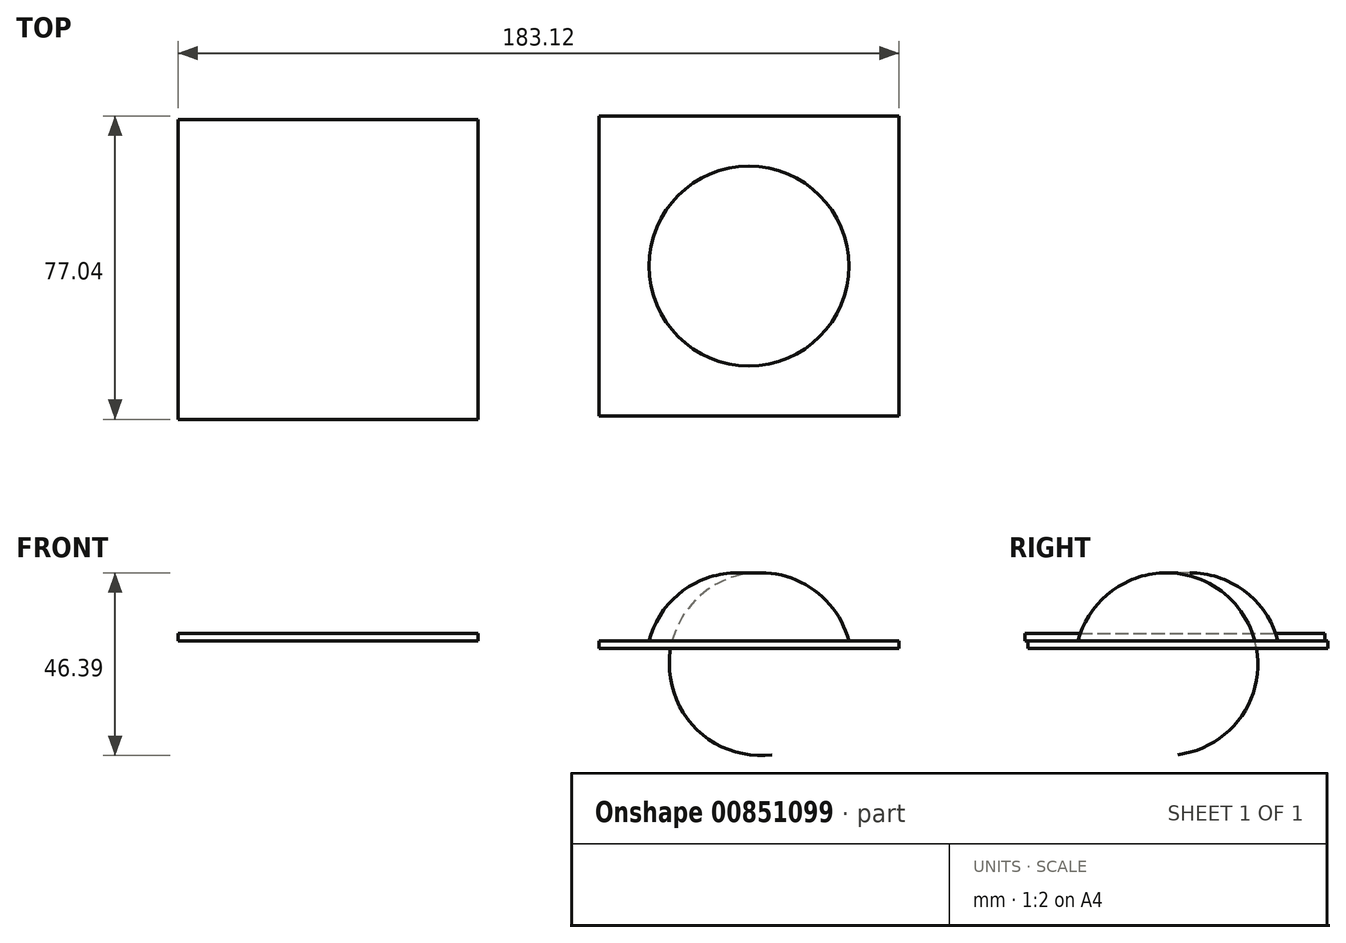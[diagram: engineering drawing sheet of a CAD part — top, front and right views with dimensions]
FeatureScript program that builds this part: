
annotation { "Feature Type Name" : "Feature", "Feature Type Description" : "" }
export const myFeature = defineFeature(function(context is Context, id is Id, definition is map)
    precondition{}
    {
        {
            var Q0;
            Q0=qCreatedBy(makeId("Front.planeOp"),FACE);
            var sketch = newSketch(context, id + "F0", { "sketchPlane" : qUnion([Q0])});
            skLineSegment(sketch, "E0", {"start": v(0, 0) * mm, "end": v(0, 17.15) * mm});
            skLineSegment(sketch, "E1", {"start": v(0, 0) * mm, "end": v(25.4, 0) * mm});
            skArc(sketch, "E2", {"start": v(25.4, 0) * mm, "mid": v(15.93, 13.36) * mm, "end": v(0, 17.14) * mm});
            skLineSegment(sketch, "E3", {"start": v(0, 75.89) * mm, "end": v(0, -74.12) * mm, "construction": true});
            skSolve(sketch);
        }
        {
            var Q0;
            Q0=makeQuery(id+"F0.imprint","IMPRINT",FACE,{"disambiguationData":[TD([[makeQuery(id+"F0.imprint","IMPRINT",EDGE,{"derivedFrom":sQuery(id+"F0.wireOp",EDGE,"E0")}),-1.0]])]});
            var Q1;
            Q1=sQuery(id+"F0.wireOp",EDGE,"E3");
            revolve(context, id + "F1", {"surfaceOperationType" : NewSurfaceOperationType.NEW, "entities" : qUnion([Q0]), "axis" : qUnion([Q1]), "revolveType" : RevolveType.FULL});
        }
        {
            var Q0;
            Q0=qCreatedBy(makeId("Top.planeOp"),FACE);
            var sketch = newSketch(context, id + "F2", { "sketchPlane" : qUnion([Q0])});
            skLineSegment(sketch, "E4.bottom", {"start": v(38.1, -38.1) * mm, "end": v(-38.1, -38.1) * mm});
            skLineSegment(sketch, "E4.top", {"start": v(38.1, 38.1) * mm, "end": v(-38.1, 38.1) * mm});
            skLineSegment(sketch, "E4.left", {"start": v(38.1, -38.1) * mm, "end": v(38.1, 38.1) * mm});
            skLineSegment(sketch, "E4.right", {"start": v(-38.1, -38.1) * mm, "end": v(-38.1, 38.1) * mm});
            skPoint(sketch, "E4.middle", {"position": v(0, 0) * mm});
            skSolve(sketch);
        }
        {
            assignVariable(context, id + "F3", {"name" : "th", "anyValue" : 1.9 * mm});
        }
        {
            var Q0;
            Q0=makeQuery(id+"F2.imprint","IMPRINT",FACE,{"disambiguationData":[TD([[makeQuery(id+"F2.imprint","IMPRINT",EDGE,{"derivedFrom":sQuery(id+"F2.wireOp",EDGE,"E4.bottom")}),-1.0]])]});
            extrude(context, id + "F4", {"entities" : qUnion([Q0]), "operationType" : NewBodyOperationType.ADD, "oppositeDirection" : true, "depth" : getVariable(context, 'th'), "offsetDistance" : 25.4 * mm});
        }
        {
            var Q0;
            Q0=qCreatedBy(makeId("Top.planeOp"),FACE);
            var sketch = newSketch(context, id + "F5", { "sketchPlane" : qUnion([Q0])});
            skLineSegment(sketch, "E5.bottom", {"start": v(-145.02, -38.94) * mm, "end": v(-68.82, -38.94) * mm});
            skLineSegment(sketch, "E5.top", {"start": v(-145.02, 37.26) * mm, "end": v(-68.82, 37.26) * mm});
            skLineSegment(sketch, "E5.left", {"start": v(-145.02, -38.94) * mm, "end": v(-145.02, 37.26) * mm});
            skLineSegment(sketch, "E5.right", {"start": v(-68.82, -38.94) * mm, "end": v(-68.82, 37.26) * mm});
            skSolve(sketch);
        }
        {
            var Q0;
            Q0=makeQuery(id+"F5.imprint","IMPRINT",FACE,{"disambiguationData":[TD([[makeQuery(id+"F5.imprint","IMPRINT",EDGE,{"derivedFrom":sQuery(id+"F5.wireOp",EDGE,"E5.bottom")}),1.0]])]});
            extrude(context, id + "F6", {"entities" : qUnion([Q0]), "depth" : getVariable(context, 'th'), "offsetDistance" : 25.4 * mm});
        }
    });
